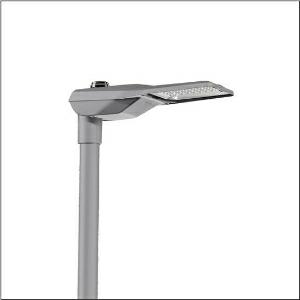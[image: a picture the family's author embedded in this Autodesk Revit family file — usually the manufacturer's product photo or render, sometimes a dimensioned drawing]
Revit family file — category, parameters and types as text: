
# Revit family: streetlight_sl_21_mini___stw1_0a_5xe6e37n08hb_09ef
name_source: partatom
category: Lighting Fixtures
units: mm (PartAtom-declared; Revit-internal decimal feet)

## family parameters
Cut with Voids When Loaded = No
Host = Face
Light Source = No
Part Type = Normal
Room Calculation Point = No
Round Connector Dimension = Use Diameter
Shared = No

## types (1)
- --- (1 x LED, 9040 lm, 66 W, 3000K)
    Apparent Load = 66 VA
    CIE Flux Codes = 38 75 98 100 100
    Color Rendering = 70
    Color Temperature = 3000K
    Default Elevation = 1800 mm
    Description = Streetlight SL 21 mini, mast luminaire, primary light control with lens, of PMMA, primary optical cover: cover, of toughened safety glass, transparent, light distribution: STW1.0a, light emission: direct distribution, primary light characteristic: asymmetric, installation type: side-entry, LED, 3G 1.5mm², High Power LED, rated luminous flux: 9.040lm, luminous efficacy: 137lm/W, light colour: 730, colour temperature: 3000K, control gear: NEMA (7pin), control: overheat protection, pre-setting: linear dimming characteristic, constant luminous flux control, time-dependent luminous flux control, flexible luminous flux parameterisation, mains connection: 230..240V, AC, 50/60Hz, connection cable pre-assembled, cable length: 8,5m, wiring characteristics: H07RN-F, start of lifetime: 66W, end of service life: 69W, reduction: 30W, luminaire housing, of diecast aluminium (EN AC-44300), powder-coated, SITECO metallic grey (DB 702S), corrosivity category C5 high according to DIN EN ISO 12944, multi-level sealing system, sealing non-destructively replaceable, inclination adjustable: 0°, 5°, 10°, 15°, length: 628mm, width: 235mm, height: 110mm, spigot size: 42mm (side-entry), mounting height: 4..8m, protection rating (complete): IP66, insulation class (complete): insulation class I (protective earthing), certification: CE, ENEC, ENEC+, VDE, impact resistance: IK10, permissible operating ambient temperature for outdoor applications: -40..+50°C, standard-compliant lighting for roads and squares, packaging unit: 1 piece

Light Distribution: STW1.0a
    Height = 110 mm
    Lamp = 1 x LED
    Lamp Light Flux = 9040 lm
    Lamp Power = 66 W
    Lamp count = 1
    Length = 625 mm
    Luminous efficacy = 137 lm/W
    Manufacturer = Siteco
    ModVariant = No
    Model = 5XE6E37N08HB
    Number of Poles = 1
    OnlyDefault = Yes
    Power Factor = 1
    Product Name = Streetlight SL 21 mini | STW1.0a
    Product group = mast luminaire | pylon top
    ProductGroupID = 6100
    Protection Class = Protection class I
    Protection Degree = IP 66
    RLX_Detail_Level = 1
    RLX_Emergency_Light_Flux = 0 lm
    RLX_Emergency_Type = 0
    RLX_Emergency_Type_DB = No
    RlxData = <blob elided: 26169 chars, md5=eba41100>
    Socket = socket
    Standby Power = 0 W
    System Light Flux = 9040 lm
    System Power = 66 W
    Type Comments = factory setting: luminous flux: 100 % | dim-lin: 254 | 670 mA
    Type Image = l_1294379.jpg
    URL = http://relux.com
    VarID = @adj_135171
    Voltage = 0 V
    Weight = 0.00 kg
    Width = 234 mm

## geometry (parser evidence)
native form markers: Blend x4, Sweep x13
no freeform markers — native parametric forms only
